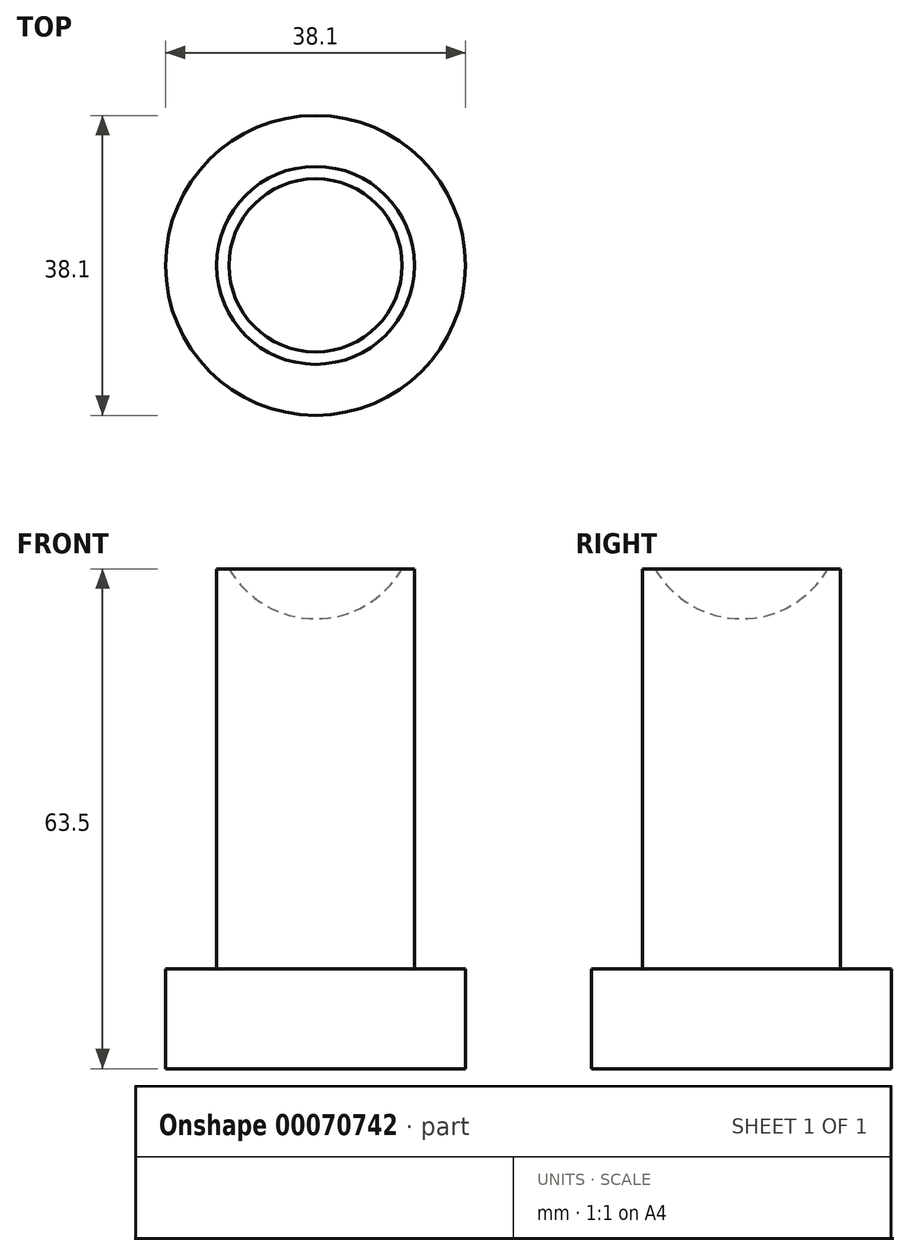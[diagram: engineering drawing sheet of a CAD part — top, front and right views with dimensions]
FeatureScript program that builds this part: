
annotation { "Feature Type Name" : "Feature", "Feature Type Description" : "" }
export const myFeature = defineFeature(function(context is Context, id is Id, definition is map)
    precondition{}
    {
        {
            var Q0;
            Q0=qCreatedBy(makeId("Top.planeOp"),FACE);
            var sketch = newSketch(context, id + "F0", { "sketchPlane" : qUnion([Q0])});
            skCircle(sketch, "E0", {"center": v(0, 0) * mm, "radius": 19.05 * mm});
            skSolve(sketch);
        }
        {
            var Q0;
            Q0 = qSketchRegion(id + "F0", true);
            extrude(context, id + "F1", {"entities" : qUnion([Q0]), "depth" : 12.7 * mm});
        }
        {
            var Q0;
            Q0=qCreatedBy(makeId("Top.planeOp"),FACE);
            var sketch = newSketch(context, id + "F2", { "sketchPlane" : qUnion([Q0])});
            skCircle(sketch, "E1", {"center": v(0, 0) * mm, "radius": 12.57 * mm});
            skSolve(sketch);
        }
        {
            var Q0;
            Q0=makeQuery(id+"F2.imprint","IMPRINT",FACE,{"disambiguationData":[TD([[makeQuery(id+"F2.imprint","IMPRINT",EDGE,{"derivedFrom":sQuery(id+"F2.wireOp",EDGE,"E1")}),1.0]])]});
            extrude(context, id + "F3", {"entities" : qUnion([Q0]), "operationType" : NewBodyOperationType.ADD, "depth" : 63.5 * mm});
        }
        {
            var Q0;
            Q0=qCreatedBy(makeId("Right.planeOp"),FACE);
            var sketch = newSketch(context, id + "F4", { "sketchPlane" : qUnion([Q0])});
            skLineSegment(sketch, "E2", {"start": v(-25.48, 69.85) * mm, "end": v(18.26, 69.85) * mm});
            skArc(sketch, "E3", {"start": v(-12.7, 69.85) * mm, "mid": v(0, 57.15) * mm, "end": v(12.7, 69.85) * mm});
            skSolve(sketch);
        }
        {
            var Q0;
            Q0=qCreatedBy(makeId("Right.planeOp"),FACE);
            var sketch = newSketch(context, id + "F5", { "sketchPlane" : qUnion([Q0])});
            skLineSegment(sketch, "E4", {"start": v(-26.74, 69.85) * mm, "end": v(23.51, 69.85) * mm});
            skSolve(sketch);
        }
        {
            var Q0;
            {var subQ0=sQuery(id+"F4.wireOp",EDGE,"E3");Q0=makeQuery(id+"F4.imprint","IMPRINT",FACE,{"disambiguationData":[TD([[makeQuery(id+"F4.imprint","IMPRINT",EDGE,{"derivedFrom":subQ0}),1.0]])]});}
            var Q1;
            Q1=sQuery(id+"F5.wireOp",EDGE,"E4");
            revolve(context, id + "F6", {"operationType" : NewBodyOperationType.REMOVE, "entities" : qUnion([Q0]), "axis" : qUnion([Q1]), "revolveType" : RevolveType.FULL, "oppositeDirection" : true});
        }
    });
